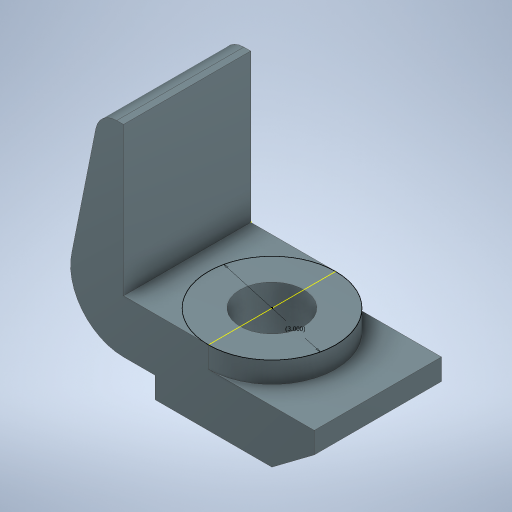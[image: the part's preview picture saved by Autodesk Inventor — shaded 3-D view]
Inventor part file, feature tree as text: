
AUTODESK INVENTOR PART (.ipt)
format: ipt  version: 2024 (Build 280153000, 153)  size: 434,176 bytes
history: native  units: in
note: dims shown in document units (in); Inventor stores cm internally (conversion verified against a paired STEP export)
features: extrude x2, other x2, hole x1, sketch x1
ambient origin geometry x8: Origin, YZ Plane, XZ Plane, XY Plane, X Axis, Y Axis, Z Axis, Center Point
bodies: Solid1 (feature_tree)
feature tree (6):
  extrude  "FULL EXTRUSION"  Depth=0.5in
  extrude  "Half Circle Extrusion"  Depth=0.5in
  hole  "Hole2"  [1 undecoded]
  other  "main profile"
  other  "Half Circle"
  sketch  "Sketch6"  dims[d8=2.0in d9=0.5in d11=2.75in d15=4.5in d16=0.5in d18=1.75in d20=0.75in d21=2.5in d23=3.0in d24=0.0in d39=0.25in d41=0.5in d42=1.25in d44=1.25in d45=4.75in d46=1.0in d47=0.0in d48=1.5in d49=0.75in d50=0.375in d51=0.25in d52=0.5635in d53=1.0in d54=0.8108in d55=3.0in d56=0.0344in d57=0.5in d58=0.0344in]
note: 1 required parameter value undecoded (feature->parameter linkage not recoverable at this tier; creation-order binding heuristic only, values carry confidence <= 0.55)
